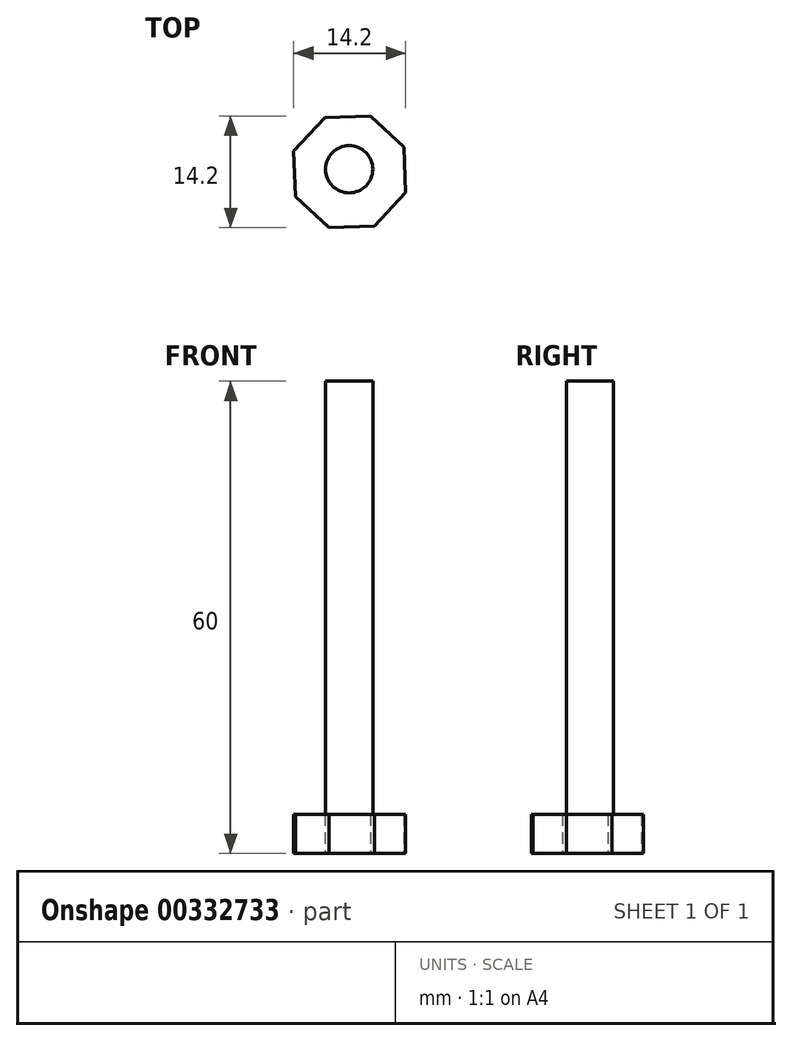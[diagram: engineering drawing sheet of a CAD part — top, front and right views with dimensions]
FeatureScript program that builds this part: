
annotation { "Feature Type Name" : "Feature", "Feature Type Description" : "" }
export const myFeature = defineFeature(function(context is Context, id is Id, definition is map)
    precondition{}
    {
        {
            var Q0;
            Q0=qCreatedBy(makeId("Top.planeOp"),FACE);
            var sketch = newSketch(context, id + "F0", { "sketchPlane" : qUnion([Q0])});
            skCircle(sketch, "E0", {"center": v(-1.75, 3.1) * mm, "radius": 3 * mm});
            skSolve(sketch);
        }
        {
            var Q0;
            Q0 = qSketchRegion(id + "F0", true);
            extrude(context, id + "F1", {"entities" : qUnion([Q0]), "depth" : 60 * mm});
        }
        {
            var Q0;
            Q0=qCreatedBy(makeId("Top.planeOp"),FACE);
            var sketch = newSketch(context, id + "F2", { "sketchPlane" : qUnion([Q0])});
            skCircle(sketch, "E1.cCircle", {"center": v(-1.69, 2.77) * mm, "radius": 7 * mm, "construction": true});
            skLineSegment(sketch, "E1.0", {"start": v(0.95, 9.87) * mm, "end": v(5.2, 5.92) * mm});
            skLineSegment(sketch, "E1.1", {"start": v(5.2, 5.92) * mm, "end": v(5.41, 0.12) * mm});
            skLineSegment(sketch, "E1.2", {"start": v(5.41, 0.12) * mm, "end": v(1.46, -4.12) * mm});
            skLineSegment(sketch, "E1.3", {"start": v(1.46, -4.12) * mm, "end": v(-4.33, -4.33) * mm});
            skLineSegment(sketch, "E1.4", {"start": v(-4.33, -4.33) * mm, "end": v(-8.58, -0.38) * mm});
            skLineSegment(sketch, "E1.5", {"start": v(-8.58, -0.38) * mm, "end": v(-8.8, 5.41) * mm});
            skLineSegment(sketch, "E1.6", {"start": v(-8.8, 5.41) * mm, "end": v(-4.84, 9.66) * mm});
            skLineSegment(sketch, "E1.7", {"start": v(-4.84, 9.66) * mm, "end": v(0.95, 9.87) * mm});
            skPoint(sketch, "E1.0.midPoint", {"position": v(3.08, 7.9) * mm});
            skSolve(sketch);
        }
        {
            var Q0;
            Q0 = qSketchRegion(id + "F2", true);
            extrude(context, id + "F3", {"entities" : qUnion([Q0]), "operationType" : NewBodyOperationType.ADD, "depth" : 5 * mm});
        }
    });
